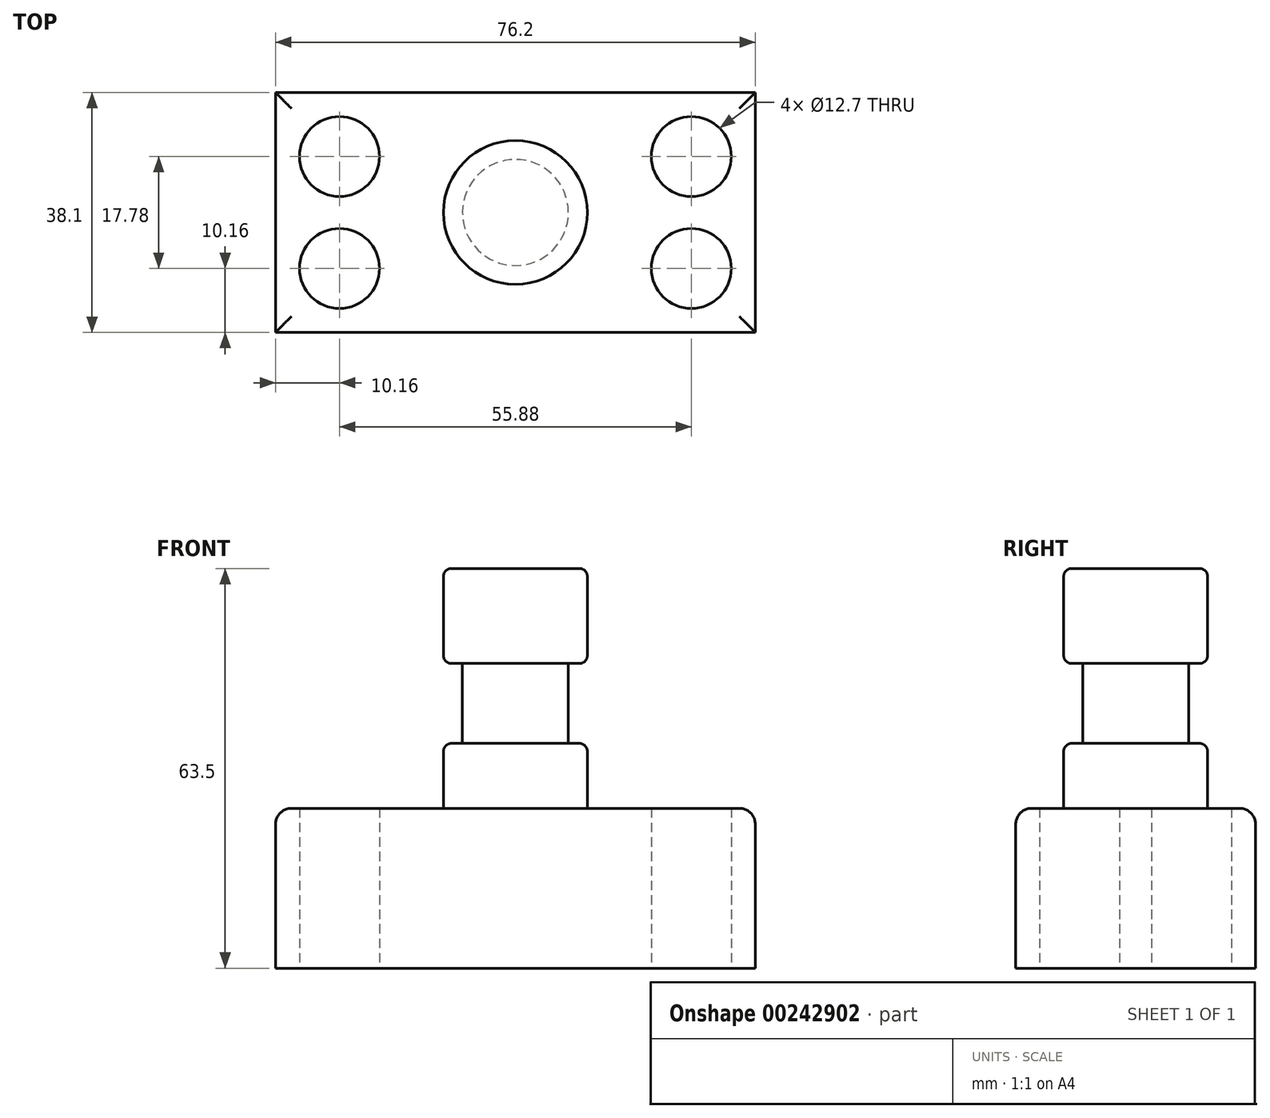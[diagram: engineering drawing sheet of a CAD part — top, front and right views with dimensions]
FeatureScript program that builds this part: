
annotation { "Feature Type Name" : "Feature", "Feature Type Description" : "" }
export const myFeature = defineFeature(function(context is Context, id is Id, definition is map)
    precondition{}
    {
        {
            var Q0;
            Q0=qCreatedBy(makeId("Top.planeOp"),FACE);
            var sketch = newSketch(context, id + "F0", { "sketchPlane" : qUnion([Q0])});
            skLineSegment(sketch, "E0.bottom", {"start": v(38.1, 19.05) * mm, "end": v(-38.1, 19.05) * mm});
            skLineSegment(sketch, "E0.top", {"start": v(38.1, -19.05) * mm, "end": v(-38.1, -19.05) * mm});
            skLineSegment(sketch, "E0.left", {"start": v(38.1, 19.05) * mm, "end": v(38.1, -19.05) * mm});
            skLineSegment(sketch, "E0.right", {"start": v(-38.1, 19.05) * mm, "end": v(-38.1, -19.05) * mm});
            skPoint(sketch, "E0.middle", {"position": v(0, 0) * mm});
            skSolve(sketch);
        }
        {
            var Q0;
            Q0 = qSketchRegion(id + "F0", true);
            extrude(context, id + "F1", {"entities" : qUnion([Q0]), "depth" : 25.4 * mm});
        }
        {
            var Q0;
            Q0=qCreatedBy(makeId("Top.planeOp"),FACE);
            var sketch = newSketch(context, id + "F2", { "sketchPlane" : qUnion([Q0])});
            skCircle(sketch, "E1", {"center": v(-27.94, 8.9) * mm, "radius": 6.35 * mm});
            skCircle(sketch, "E2", {"center": v(27.94, 8.9) * mm, "radius": 6.35 * mm});
            skCircle(sketch, "E3", {"center": v(-27.94, -8.9) * mm, "radius": 6.35 * mm});
            skCircle(sketch, "E4", {"center": v(27.94, -8.9) * mm, "radius": 6.35 * mm});
            skSolve(sketch);
        }
        {
            var Q0;
            Q0 = qSketchRegion(id + "F2", true);
            extrude(context, id + "F3", {"entities" : qUnion([Q0]), "operationType" : NewBodyOperationType.REMOVE, "depth" : 25.4 * mm});
        }
        {
            var Q0;
            Q0=makeQuery(id+"F1.opExtrude","CAP_FACE",FACE,{"disambiguationData":[OSD([sQuery(id+"F0.wireOp",EDGE,"E0.bottom"),sQuery(id+"F0.wireOp",EDGE,"E0.top"),sQuery(id+"F0.wireOp",EDGE,"E0.left"),sQuery(id+"F0.wireOp",EDGE,"E0.right")])],"isStart":false});
            var sketch = newSketch(context, id + "F4", { "sketchPlane" : qUnion([Q0])});
            skCircle(sketch, "E5", {"center": v(0, 0) * mm, "radius": 11.43 * mm});
            skSolve(sketch);
        }
        {
            var Q0;
            Q0=makeQuery(id+"F4.imprint","IMPRINT",FACE,{"disambiguationData":[TD([[makeQuery(id+"F4.imprint","IMPRINT",EDGE,{"derivedFrom":sQuery(id+"F4.wireOp",EDGE,"E5")}),1.0]])]});
            var Q1;
            Q1=sQuery(id+"F4.wireOp",EDGE,"E5");
            extrude(context, id + "F5", {"entities" : qUnion([Q0]), "operationType" : NewBodyOperationType.ADD, "surfaceEntities" : qUnion([Q1]), "depth" : 38.1 * mm});
        }
        {
            var Q0;
            Q0=qCreatedBy(makeId("Front.planeOp"),FACE);
            var sketch = newSketch(context, id + "F6", { "sketchPlane" : qUnion([Q0])});
            skLineSegment(sketch, "E6.bottom", {"start": v(-8.42, 48.4) * mm, "end": v(-23.66, 48.4) * mm});
            skLineSegment(sketch, "E6.top", {"start": v(-8.42, 35.7) * mm, "end": v(-23.66, 35.7) * mm});
            skLineSegment(sketch, "E6.left", {"start": v(-8.42, 48.4) * mm, "end": v(-8.42, 35.7) * mm});
            skLineSegment(sketch, "E6.right", {"start": v(-23.66, 48.4) * mm, "end": v(-23.66, 35.7) * mm});
            skSolve(sketch);
        }
        {
            var Q0;
            Q0 = qSketchRegion(id + "F6", true);
            var Q1;
            Q1=makeQuery(id+"F5.opExtrude","SWEPT_FACE",FACE,{"disambiguationData":[OSD([sQuery(id+"F4.wireOp",EDGE,"E5")])]});
            revolve(context, id + "F7", {"operationType" : NewBodyOperationType.REMOVE, "entities" : qUnion([Q0]), "axis" : qUnion([Q1]), "revolveType" : RevolveType.FULL, "oppositeDirection" : true});
        }
        {
            var Q0;
            Q0=makeQuery(id+"F1.opExtrude","CAP_EDGE",EDGE,{"disambiguationData":[OSD([sQuery(id+"F0.wireOp",EDGE,"E0.right")])],"isStart":false});
            var Q1;
            Q1=makeQuery(id+"F1.opExtrude","CAP_EDGE",EDGE,{"disambiguationData":[OSD([sQuery(id+"F0.wireOp",EDGE,"E0.top")])],"isStart":false});
            var Q2;
            Q2=makeQuery(id+"F1.opExtrude","CAP_EDGE",EDGE,{"disambiguationData":[OSD([sQuery(id+"F0.wireOp",EDGE,"E0.left")])],"isStart":false});
            var Q3;
            Q3=makeQuery(id+"F1.opExtrude","CAP_EDGE",EDGE,{"disambiguationData":[OSD([sQuery(id+"F0.wireOp",EDGE,"E0.bottom")])],"isStart":false});
            fillet(context, id + "F8", {"entities" : qUnion([Q0, Q1, Q2, Q3]), "radius" : 2.54 * mm, "tangentPropagation" : true, "allowEdgeOverflow" : false});
        }
        {
            var Q0;
            Q0=makeQuery(id+"F5.opExtrude","CAP_EDGE",EDGE,{"disambiguationData":[OSD([sQuery(id+"F4.wireOp",EDGE,"E5")])],"isStart":false});
            var Q1;
            Q1=makeQuery(id+"F7.boolean.opBoolean","INTERSECT",EDGE,{"derivedFrom":[makeQuery(id+"F5.opExtrude","SWEPT_FACE",FACE,{"disambiguationData":[OSD([sQuery(id+"F4.wireOp",EDGE,"E5")])]}),makeQuery(id+"F7.opRevolve","SWEPT_FACE",FACE,{"disambiguationData":[OSD([sQuery(id+"F6.wireOp",EDGE,"E6.top")])]})]});
            var Q2;
            Q2=makeQuery(id+"F7.boolean.opBoolean","INTERSECT",EDGE,{"derivedFrom":[makeQuery(id+"F5.opExtrude","SWEPT_FACE",FACE,{"disambiguationData":[OSD([sQuery(id+"F4.wireOp",EDGE,"E5")])]}),makeQuery(id+"F7.opRevolve","SWEPT_FACE",FACE,{"disambiguationData":[OSD([sQuery(id+"F6.wireOp",EDGE,"E6.bottom")])]})]});
            var Q3;
            Q3=makeQuery(id+"F5.opExtrude","CAP_EDGE",EDGE,{"disambiguationData":[OSD([sQuery(id+"F4.wireOp",EDGE,"E5")])],"isStart":true});
            fillet(context, id + "F9", {"entities" : qUnion([Q0, Q1, Q2, Q3]), "radius" : 1.27 * mm, "tangentPropagation" : true, "allowEdgeOverflow" : false});
        }
    });
